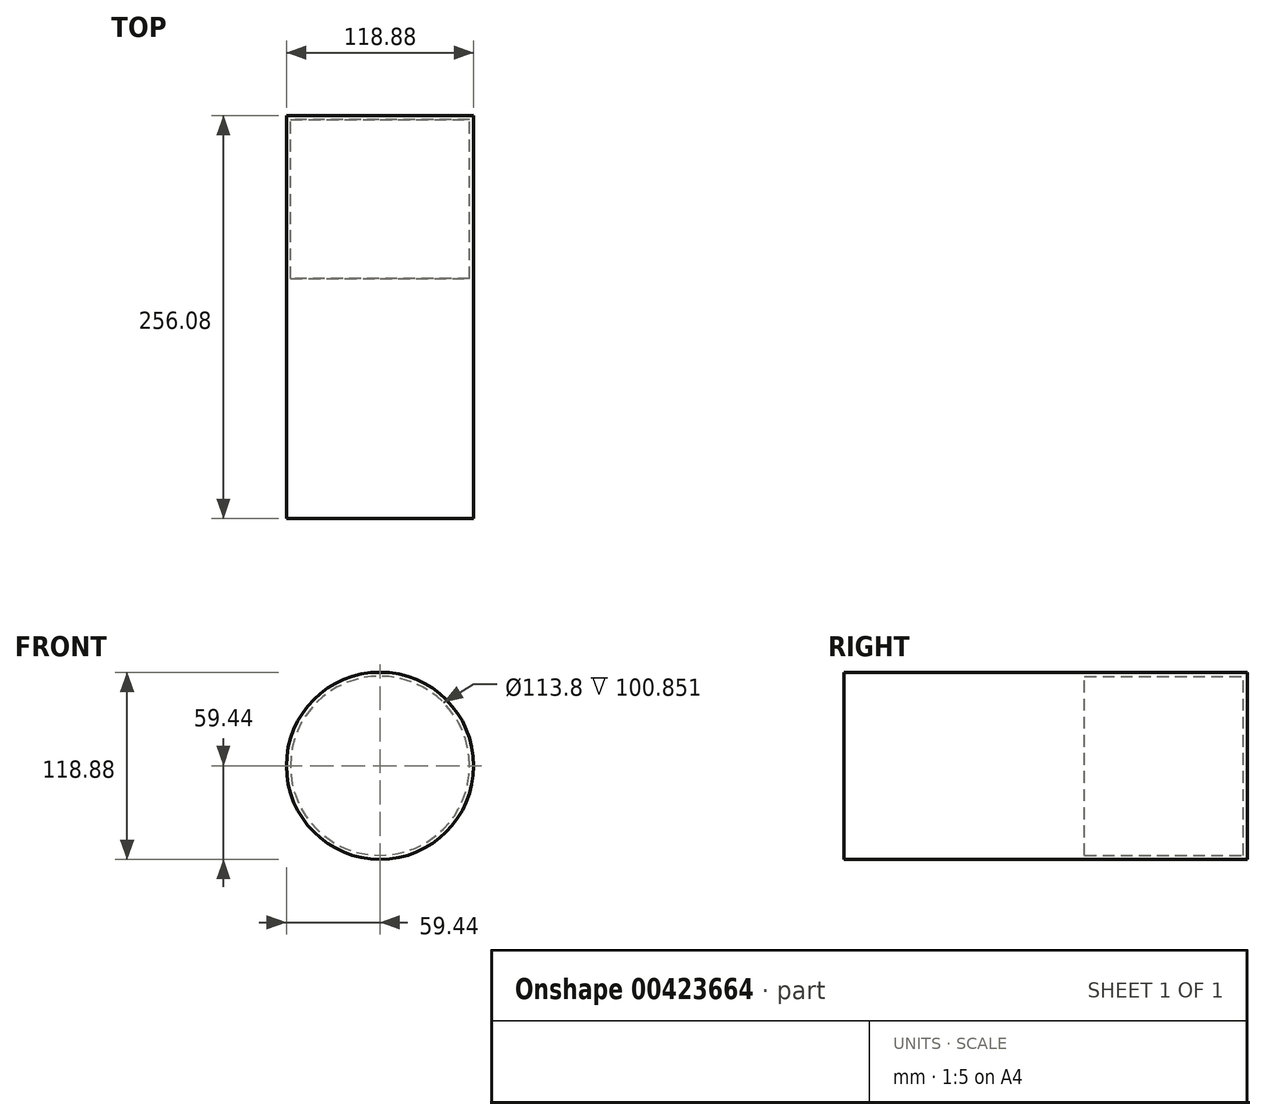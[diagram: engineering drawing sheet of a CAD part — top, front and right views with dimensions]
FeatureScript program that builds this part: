
annotation { "Feature Type Name" : "Feature", "Feature Type Description" : "" }
export const myFeature = defineFeature(function(context is Context, id is Id, definition is map)
    precondition{}
    {
        {
            var Q0;
            Q0=qCreatedBy(makeId("Front.planeOp"),FACE);
            var sketch = newSketch(context, id + "F0", { "sketchPlane" : qUnion([Q0])});
            skCircle(sketch, "E0", {"center": v(0, 0) * mm, "radius": 56.9 * mm});
            skSolve(sketch);
        }
        {
            var Q0;
            Q0=makeQuery(id+"F0.imprint","IMPRINT",FACE,{"disambiguationData":[TD([[makeQuery(id+"F0.imprint","IMPRINT",EDGE,{"derivedFrom":sQuery(id+"F0.wireOp",EDGE,"E0")}),1.0]])]});
            var sketch = newSketch(context, id + "F1", { "sketchPlane" : qUnion([Q0])});
            skSolve(sketch);
        }
        {
            var Q0;
            Q0=makeQuery(id+"F1.imprint","IMPRINT",FACE,{"disambiguationData":[TD([[makeQuery(id+"F1.imprint","IMPRINT",EDGE,{"derivedFrom":makeQuery(id+"F0.imprint","IMPRINT",EDGE,{"derivedFrom":sQuery(id+"F0.wireOp",EDGE,"E0")})}),1.0]])]});
            extrude(context, id + "F2", {"entities" : qUnion([Q0]), "depth" : 100.85 * mm});
        }
        {
            var Q0;
            Q0=makeQuery(id+"F2.opExtrude","CAP_FACE",FACE,{"disambiguationData":[OSD([sQuery(id+"F0.wireOp",EDGE,"E0")])],"isStart":false});
            var Q1;
            Q1=makeQuery(id+"F2.opExtrude","SWEPT_BODY",BODY,{"disambiguationData":[OSD([sQuery(id+"F0.wireOp",EDGE,"E0")])]});
            shell(context, id + "F3", {"isHollow" : true, "entities" : qUnion([Q0]), "parts" : qUnion([Q1]), "thickness" : 2.54 * mm, "oppositeDirection" : true});
        }
        {
            var Q0;
            Q0=makeQuery(id+"F2.opExtrude","CAP_FACE",FACE,{"disambiguationData":[OSD([sQuery(id+"F0.wireOp",EDGE,"E0")])],"isStart":false});
            extrude(context, id + "F4", {"entities" : qUnion([Q0]), "operationType" : NewBodyOperationType.ADD, "depth" : 150.15 * mm});
        }
    });
